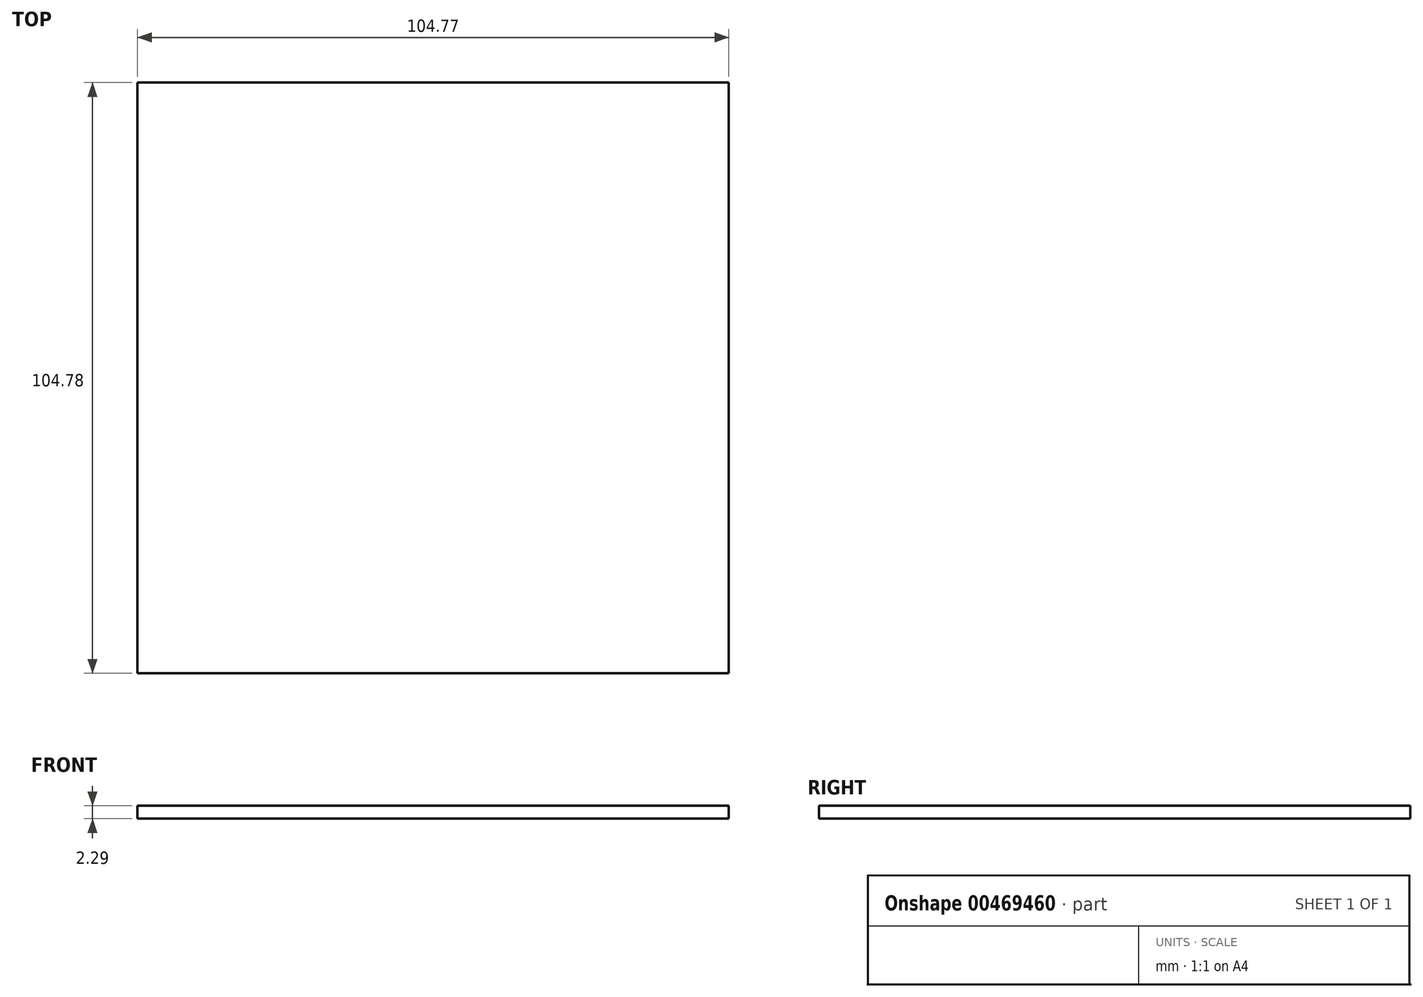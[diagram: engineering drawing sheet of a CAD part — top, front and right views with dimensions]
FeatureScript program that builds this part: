
annotation { "Feature Type Name" : "Feature", "Feature Type Description" : "" }
export const myFeature = defineFeature(function(context is Context, id is Id, definition is map)
    precondition{}
    {
        {
            var Q0;
            Q0=qCreatedBy(makeId("Top.planeOp"),FACE);
            var sketch = newSketch(context, id + "F0", { "sketchPlane" : qUnion([Q0])});
            skLineSegment(sketch, "E0.bottom", {"start": v(-59.13, 67.44) * mm, "end": v(45.64, 67.44) * mm});
            skLineSegment(sketch, "E0.top", {"start": v(-59.13, -37.34) * mm, "end": v(45.64, -37.34) * mm});
            skLineSegment(sketch, "E0.left", {"start": v(-59.13, 67.44) * mm, "end": v(-59.13, -37.34) * mm});
            skLineSegment(sketch, "E0.right", {"start": v(45.64, 67.44) * mm, "end": v(45.64, -37.34) * mm});
            skSolve(sketch);
        }
        {
            var Q0;
            Q0=makeQuery(id+"F0.imprint","IMPRINT",FACE,{"disambiguationData":[TD([[makeQuery(id+"F0.imprint","IMPRINT",EDGE,{"derivedFrom":sQuery(id+"F0.wireOp",EDGE,"E0.bottom")}),-1.0]])]});
            extrude(context, id + "F1", {"entities" : qUnion([Q0]), "depth" : 2.3 * mm});
        }
    });
